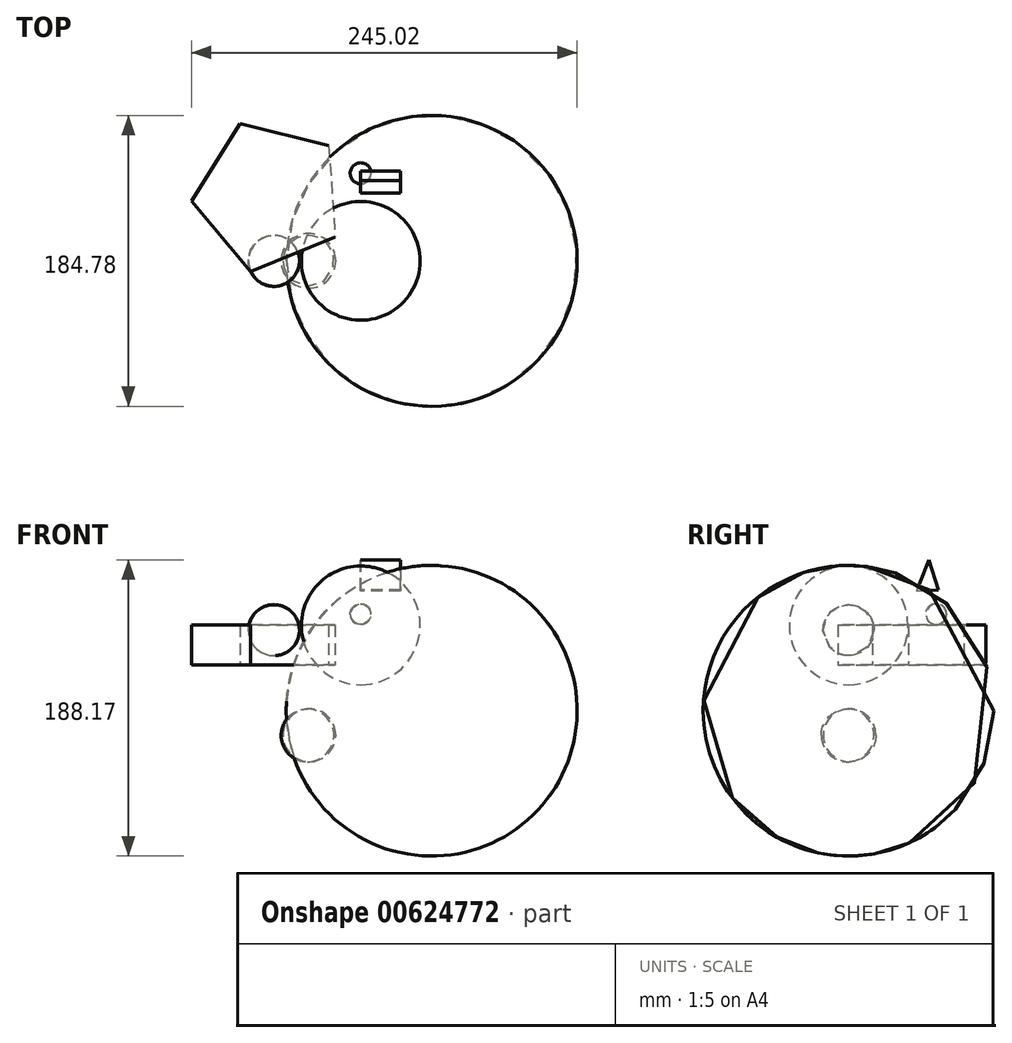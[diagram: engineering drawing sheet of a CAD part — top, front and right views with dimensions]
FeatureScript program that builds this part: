
annotation { "Feature Type Name" : "Feature", "Feature Type Description" : "" }
export const myFeature = defineFeature(function(context is Context, id is Id, definition is map)
    precondition{}
    {
        {
            var Q0;
            Q0=qCreatedBy(makeId("Front.planeOp"),FACE);
            var sketch = newSketch(context, id + "F0", { "sketchPlane" : qUnion([Q0])});
            skCircle(sketch, "E0", {"center": v(0, 25.28) * mm, "radius": 37.7 * mm});
            skLineSegment(sketch, "E1", {"start": v(0, 71.99) * mm, "end": v(0, -27.72) * mm});
            skSolve(sketch);
        }
        {
            var Q0;
            {var subQ0=sQuery(id+"F0.wireOp",EDGE,"E1");var subQ1=sQuery(id+"F0.wireOp",EDGE,"E0");var subQ2=makeQuery(id+"F0.imprint","INTERSECT",VERTEX,{"disambiguationData":[OD(0.0)],"derivedFrom":[subQ1,subQ0]});Q0=makeQuery(id+"F0.imprint","IMPRINT",FACE,{"disambiguationData":[TD([[makeQuery(id+"F0.imprint","IMPRINT",EDGE,{"disambiguationData":[TD([[subQ2,1.0]])],"derivedFrom":subQ1}),1.0]])]});}
            var Q1;
            Q1=sQuery(id+"F0.wireOp",EDGE,"E1");
            revolve(context, id + "F1", {"entities" : qUnion([Q0]), "axis" : qUnion([Q1]), "revolveType" : RevolveType.FULL});
        }
        {
            var Q0;
            Q0=qCreatedBy(makeId("Front.planeOp"),FACE);
            var sketch = newSketch(context, id + "F2", { "sketchPlane" : qUnion([Q0])});
            skCircle(sketch, "E2", {"center": v(-55.13, 22.24) * mm, "radius": 16.18 * mm});
            skLineSegment(sketch, "E3", {"start": v(-56.56, 48.43) * mm, "end": v(-52.9, -18.58) * mm});
            skSolve(sketch);
        }
        {
            var Q0;
            {var subQ0=sQuery(id+"F2.wireOp",EDGE,"E3");var subQ1=sQuery(id+"F2.wireOp",EDGE,"E2");var subQ2=makeQuery(id+"F2.imprint","INTERSECT",VERTEX,{"disambiguationData":[OD(0.0)],"derivedFrom":[subQ1,subQ0]});Q0=makeQuery(id+"F2.imprint","IMPRINT",FACE,{"disambiguationData":[TD([[makeQuery(id+"F2.imprint","IMPRINT",EDGE,{"disambiguationData":[TD([[subQ2,1.0]])],"derivedFrom":subQ1}),1.0]])]});}
            var Q1;
            Q1=sQuery(id+"F2.wireOp",EDGE,"E3");
            revolve(context, id + "F3", {"entities" : qUnion([Q0]), "axis" : qUnion([Q1]), "revolveType" : RevolveType.FULL});
        }
        {
            var Q0;
            Q0=qCreatedBy(makeId("Right.planeOp"),FACE);
            var sketch = newSketch(context, id + "F4", { "sketchPlane" : qUnion([Q0])});
            skCircle(sketch, "E4", {"center": v(55.74, 32.39) * mm, "radius": 6.56 * mm});
            skLineSegment(sketch, "E5", {"start": v(56.35, 45.39) * mm, "end": v(54.52, 13.1) * mm});
            skSolve(sketch);
        }
        {
            var Q0;
            {var subQ0=sQuery(id+"F4.wireOp",EDGE,"E5");var subQ1=sQuery(id+"F4.wireOp",EDGE,"E4");var subQ2=makeQuery(id+"F4.imprint","INTERSECT",VERTEX,{"disambiguationData":[OD(0.0)],"derivedFrom":[subQ1,subQ0]});Q0=makeQuery(id+"F4.imprint","IMPRINT",FACE,{"disambiguationData":[TD([[makeQuery(id+"F4.imprint","IMPRINT",EDGE,{"disambiguationData":[TD([[subQ2,1.0]])],"derivedFrom":subQ1}),1.0]])]});}
            var Q1;
            Q1=sQuery(id+"F4.wireOp",EDGE,"E5");
            revolve(context, id + "F5", {"entities" : qUnion([Q0]), "axis" : qUnion([Q1]), "revolveType" : RevolveType.FULL});
        }
        {
            var Q0;
            Q0=qCreatedBy(makeId("Right.planeOp"),FACE);
            var sketch = newSketch(context, id + "F6", { "sketchPlane" : qUnion([Q0])});
            skLineSegment(sketch, "E6", {"start": v(57.16, 47.82) * mm, "end": v(50.87, 66.91) * mm});
            skLineSegment(sketch, "E7", {"start": v(50.87, 66.91) * mm, "end": v(43.15, 47.01) * mm});
            skLineSegment(sketch, "E8", {"start": v(43.15, 47.01) * mm, "end": v(57.16, 47.82) * mm});
            skSolve(sketch);
        }
        {
            var Q0;
            Q0 = qSketchRegion(id + "F6", true);
            extrude(context, id + "F7", {"entities" : qUnion([Q0]), "depth" : 25.4 * mm, "offsetDistance" : 25.4 * mm});
        }
        {
            var Q0;
            Q0=qCreatedBy(makeId("Front.planeOp"),FACE);
            var sketch = newSketch(context, id + "F8", { "sketchPlane" : qUnion([Q0])});
            skCircle(sketch, "E9", {"center": v(-32.6, -44.57) * mm, "radius": 16.75 * mm});
            skLineSegment(sketch, "E10", {"start": v(-33.2, -16.75) * mm, "end": v(-33.2, -75.44) * mm});
            skSolve(sketch);
        }
        {
            var Q0;
            {var subQ0=sQuery(id+"F8.wireOp",EDGE,"E10");var subQ1=sQuery(id+"F8.wireOp",EDGE,"E9");var subQ2=makeQuery(id+"F8.imprint","INTERSECT",VERTEX,{"disambiguationData":[OD(0.0)],"derivedFrom":[subQ1,subQ0]});Q0=makeQuery(id+"F8.imprint","IMPRINT",FACE,{"disambiguationData":[TD([[makeQuery(id+"F8.imprint","IMPRINT",EDGE,{"disambiguationData":[TD([[subQ2,-1.0]])],"derivedFrom":subQ1}),1.0]])]});}
            var Q1;
            Q1=sQuery(id+"F8.wireOp",EDGE,"E10");
            revolve(context, id + "F9", {"entities" : qUnion([Q0]), "axis" : qUnion([Q1]), "revolveType" : RevolveType.FULL});
        }
        {
            var Q0;
            Q0=qCreatedBy(makeId("Front.planeOp"),FACE);
            var sketch = newSketch(context, id + "F10", { "sketchPlane" : qUnion([Q0])});
            skCircle(sketch, "E11", {"center": v(44.98, -28.94) * mm, "radius": 92.31 * mm});
            skLineSegment(sketch, "E12", {"start": v(53.22, 95.28) * mm, "end": v(38.19, -133.54) * mm});
            skSolve(sketch);
        }
        {
            var Q0;
            {var subQ0=sQuery(id+"F10.wireOp",EDGE,"E12");var subQ1=sQuery(id+"F10.wireOp",EDGE,"E11");var subQ2=makeQuery(id+"F10.imprint","INTERSECT",VERTEX,{"disambiguationData":[OD(0.0)],"derivedFrom":[subQ1,subQ0]});Q0=makeQuery(id+"F10.imprint","IMPRINT",FACE,{"disambiguationData":[TD([[makeQuery(id+"F10.imprint","IMPRINT",EDGE,{"disambiguationData":[TD([[subQ2,1.0]])],"derivedFrom":subQ1}),1.0]])]});}
            var Q1;
            Q1=sQuery(id+"F10.wireOp",EDGE,"E12");
            revolve(context, id + "F11", {"entities" : qUnion([Q0]), "axis" : qUnion([Q1]), "revolveType" : RevolveType.FULL});
        }
        {
            var Q0;
            Q0=qCreatedBy(makeId("Top.planeOp"),FACE);
            var sketch = newSketch(context, id + "F12", { "sketchPlane" : qUnion([Q0])});
            skCircle(sketch, "E13.cCircle", {"center": v(-58.2, 41.34) * mm, "radius": 40.04 * mm, "construction": true});
            skLineSegment(sketch, "E13.0", {"start": v(-76.78, 87.21) * mm, "end": v(-20.31, 73.2) * mm});
            skLineSegment(sketch, "E13.1", {"start": v(-20.31, 73.2) * mm, "end": v(-16.2, 15.15) * mm});
            skLineSegment(sketch, "E13.2", {"start": v(-16.2, 15.15) * mm, "end": v(-70.13, -6.7) * mm});
            skLineSegment(sketch, "E13.3", {"start": v(-70.13, -6.7) * mm, "end": v(-107.57, 37.84) * mm});
            skLineSegment(sketch, "E13.4", {"start": v(-107.57, 37.84) * mm, "end": v(-76.78, 87.21) * mm});
            skPoint(sketch, "E13.0.midPoint", {"position": v(-48.55, 80.2) * mm});
            skSolve(sketch);
        }
        {
            var Q0;
            Q0 = qSketchRegion(id + "F12", true);
            extrude(context, id + "F13", {"entities" : qUnion([Q0]), "depth" : 25.4 * mm, "offsetDistance" : 25.4 * mm});
        }
    });
